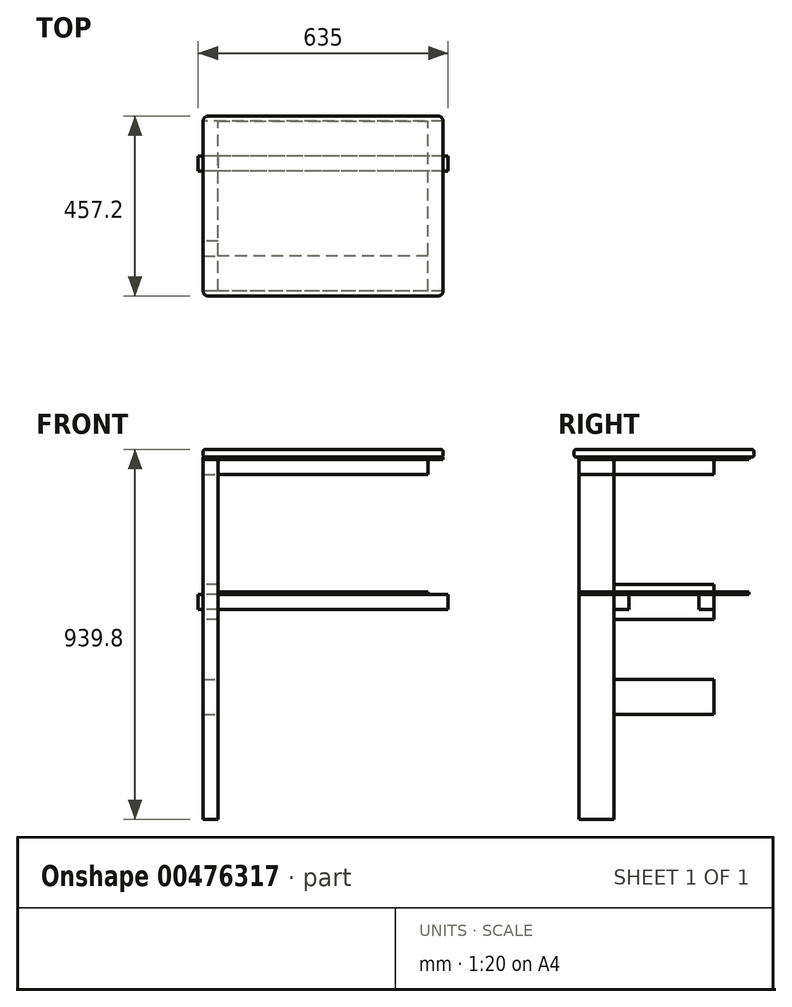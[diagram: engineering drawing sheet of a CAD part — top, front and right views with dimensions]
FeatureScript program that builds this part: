
annotation { "Feature Type Name" : "Feature", "Feature Type Description" : "" }
export const myFeature = defineFeature(function(context is Context, id is Id, definition is map)
    precondition{}
    {
        {
            var Q0;
            Q0=qCreatedBy(makeId("Top.planeOp"),FACE);
            var sketch = newSketch(context, id + "F0", { "sketchPlane" : qUnion([Q0])});
            skLineSegment(sketch, "E0.bottom", {"start": v(304.8, -215.9) * mm, "end": v(-304.8, -215.9) * mm});
            skLineSegment(sketch, "E0.top", {"start": v(304.8, 215.9) * mm, "end": v(-304.8, 215.9) * mm});
            skLineSegment(sketch, "E0.left", {"start": v(304.8, -215.9) * mm, "end": v(304.8, 215.9) * mm});
            skLineSegment(sketch, "E0.right", {"start": v(-304.8, -215.9) * mm, "end": v(-304.8, 215.9) * mm});
            skPoint(sketch, "E0.middle", {"position": v(0, 0) * mm});
            skSolve(sketch);
        }
        {
            var Q0;
            Q0 = qSketchRegion(id + "F0", true);
            extrude(context, id + "F1", {"entities" : qUnion([Q0]), "oppositeDirection" : true, "depth" : 6.35 * mm, "offsetDistance" : 25.4 * mm});
        }
        {
            var Q0;
            Q0=makeQuery(id+"F1.opExtrude","CAP_FACE",FACE,{"disambiguationData":[OSD([sQuery(id+"F0.wireOp",EDGE,"E0.bottom"),sQuery(id+"F0.wireOp",EDGE,"E0.top"),sQuery(id+"F0.wireOp",EDGE,"E0.left"),sQuery(id+"F0.wireOp",EDGE,"E0.right")])],"isStart":false});
            var sketch = newSketch(context, id + "F2", { "sketchPlane" : qUnion([Q0])});
            skLineSegment(sketch, "E1.bottom", {"start": v(-304.8, 215.9) * mm, "end": v(-266.7, 215.9) * mm});
            skLineSegment(sketch, "E1.top", {"start": v(-304.8, 127) * mm, "end": v(-266.7, 127) * mm});
            skLineSegment(sketch, "E1.left", {"start": v(-304.8, 215.9) * mm, "end": v(-304.8, 127) * mm});
            skLineSegment(sketch, "E1.right", {"start": v(-266.7, 215.9) * mm, "end": v(-266.7, 127) * mm});
            skSolve(sketch);
        }
        {
            var Q0;
            Q0 = qSketchRegion(id + "F2", true);
            extrude(context, id + "F3", {"entities" : qUnion([Q0]), "depth" : 914.4 * mm, "offsetDistance" : 25.4 * mm});
        }
        {
            var Q0;
            Q0=makeQuery(id+"F3.opExtrude","SWEPT_FACE",FACE,{"disambiguationData":[OSD([sQuery(id+"F2.wireOp",EDGE,"E1.right")])]});
            var sketch = newSketch(context, id + "F4", { "sketchPlane" : qUnion([Q0])});
            skLineSegment(sketch, "E2.bottom", {"start": v(-215.9, -6.35) * mm, "end": v(-127, -6.35) * mm});
            skLineSegment(sketch, "E2.top", {"start": v(-215.9, -44.45) * mm, "end": v(-127, -44.45) * mm});
            skLineSegment(sketch, "E2.left", {"start": v(-215.9, -6.35) * mm, "end": v(-215.9, -44.45) * mm});
            skLineSegment(sketch, "E2.right", {"start": v(-127, -6.35) * mm, "end": v(-127, -44.45) * mm});
            skSolve(sketch);
        }
        {
            var Q0;
            Q0 = qSketchRegion(id + "F4", true);
            extrude(context, id + "F5", {"entities" : qUnion([Q0]), "depth" : 533.4 * mm, "offsetDistance" : 25.4 * mm});
        }
        {
            var Q0;
            Q0=makeQuery(id+"F3.opExtrude","SWEPT_FACE",FACE,{"disambiguationData":[OSD([sQuery(id+"F2.wireOp",EDGE,"E1.top")])]});
            var sketch = newSketch(context, id + "F6", { "sketchPlane" : qUnion([Q0])});
            skLineSegment(sketch, "E3.bottom", {"start": v(304.8, -6.35) * mm, "end": v(266.7, -6.35) * mm});
            skLineSegment(sketch, "E3.top", {"start": v(304.8, -44.45) * mm, "end": v(266.7, -44.45) * mm});
            skLineSegment(sketch, "E3.left", {"start": v(304.8, -6.35) * mm, "end": v(304.8, -44.45) * mm});
            skLineSegment(sketch, "E3.right", {"start": v(266.7, -6.35) * mm, "end": v(266.7, -44.45) * mm});
            skSolve(sketch);
        }
        {
            var Q0;
            Q0 = qSketchRegion(id + "F6", true);
            extrude(context, id + "F7", {"entities" : qUnion([Q0]), "depth" : 254 * mm, "offsetDistance" : 25.4 * mm});
        }
        {
            var Q0;
            Q0=makeQuery(id+"F3.opExtrude","SWEPT_FACE",FACE,{"disambiguationData":[OSD([sQuery(id+"F2.wireOp",EDGE,"E1.top")])]});
            var sketch = newSketch(context, id + "F8", { "sketchPlane" : qUnion([Q0])});
            skLineSegment(sketch, "E4.bottom", {"start": v(304.8, -565.15) * mm, "end": v(266.7, -565.15) * mm});
            skLineSegment(sketch, "E4.top", {"start": v(304.8, -654.05) * mm, "end": v(266.7, -654.05) * mm});
            skLineSegment(sketch, "E4.left", {"start": v(304.8, -565.15) * mm, "end": v(304.8, -654.05) * mm});
            skLineSegment(sketch, "E4.right", {"start": v(266.7, -565.15) * mm, "end": v(266.7, -654.05) * mm});
            skSolve(sketch);
        }
        {
            var Q0;
            Q0 = qSketchRegion(id + "F8", true);
            extrude(context, id + "F9", {"entities" : qUnion([Q0]), "depth" : 254 * mm, "offsetDistance" : 25.4 * mm});
        }
        {
            var Q0;
            Q0=makeQuery(id+"F3.opExtrude","SWEPT_FACE",FACE,{"disambiguationData":[OSD([sQuery(id+"F2.wireOp",EDGE,"E1.left")])]});
            var sketch = newSketch(context, id + "F10", { "sketchPlane" : qUnion([Q0])});
            skLineSegment(sketch, "E5.bottom", {"start": v(127, -323.85) * mm, "end": v(-127, -323.85) * mm});
            skLineSegment(sketch, "E5.top", {"start": v(127, -412.75) * mm, "end": v(-127, -412.75) * mm});
            skLineSegment(sketch, "E5.left", {"start": v(127, -323.85) * mm, "end": v(127, -349.25) * mm});
            skLineSegment(sketch, "E5.right", {"start": v(-127, -323.85) * mm, "end": v(-127, -349.25) * mm});
            skLineSegment(sketch, "E6.bottom", {"start": v(-127, -349.25) * mm, "end": v(-88.9, -349.25) * mm});
            skLineSegment(sketch, "E6.top", {"start": v(-127, -387.35) * mm, "end": v(-88.9, -387.35) * mm});
            skLineSegment(sketch, "E6.right", {"start": v(-88.9, -349.25) * mm, "end": v(-88.9, -387.35) * mm});
            skLineSegment(sketch, "E7.bottom", {"start": v(127, -349.25) * mm, "end": v(88.9, -349.25) * mm});
            skLineSegment(sketch, "E7.top", {"start": v(127, -387.35) * mm, "end": v(88.9, -387.35) * mm});
            skLineSegment(sketch, "E7.right", {"start": v(88.9, -349.25) * mm, "end": v(88.9, -387.35) * mm});
            skLineSegment(sketch, "E8.trimOffspring", {"start": v(-127, -387.35) * mm, "end": v(-127, -412.75) * mm});
            skLineSegment(sketch, "E9.trimOffspring", {"start": v(127, -387.35) * mm, "end": v(127, -412.75) * mm});
            skSolve(sketch);
        }
        {
            var Q0;
            Q0 = qSketchRegion(id + "F10", true);
            extrude(context, id + "F11", {"entities" : qUnion([Q0]), "oppositeDirection" : true, "depth" : 38.1 * mm, "offsetDistance" : 25.4 * mm});
        }
        {
            var Q0;
            Q0=makeQuery(id+"F11.opExtrude","CAP_FACE",FACE,{"disambiguationData":[OSD([sQuery(id+"F10.wireOp",EDGE,"E5.bottom"),sQuery(id+"F10.wireOp",EDGE,"E5.top"),sQuery(id+"F10.wireOp",EDGE,"E5.left"),sQuery(id+"F10.wireOp",EDGE,"E5.right"),sQuery(id+"F10.wireOp",EDGE,"E6.bottom"),sQuery(id+"F10.wireOp",EDGE,"E6.top"),sQuery(id+"F10.wireOp",EDGE,"E6.right"),sQuery(id+"F10.wireOp",EDGE,"E7.bottom"),sQuery(id+"F10.wireOp",EDGE,"E7.top"),sQuery(id+"F10.wireOp",EDGE,"E7.right"),sQuery(id+"F10.wireOp",EDGE,"E8.trimOffspring"),sQuery(id+"F10.wireOp",EDGE,"E9.trimOffspring")])],"isStart":true});
            var sketch = newSketch(context, id + "F12", { "sketchPlane" : qUnion([Q0])});
            skLineSegment(sketch, "E10.bottom", {"start": v(-127, -349.25) * mm, "end": v(-88.9, -349.25) * mm});
            skLineSegment(sketch, "E10.top", {"start": v(-127, -387.35) * mm, "end": v(-88.9, -387.35) * mm});
            skLineSegment(sketch, "E10.left", {"start": v(-127, -349.25) * mm, "end": v(-127, -387.35) * mm});
            skLineSegment(sketch, "E10.right", {"start": v(-88.9, -349.25) * mm, "end": v(-88.9, -387.35) * mm});
            skSolve(sketch);
        }
        {
            var Q0;
            Q0 = qSketchRegion(id + "F12", true);
            extrude(context, id + "F13", {"entities" : qUnion([Q0]), "oppositeDirection" : true, "depth" : 622.3 * mm, "offsetDistance" : 25.4 * mm, "hasSecondDirection" : true, "secondDirectionOppositeDirection" : false, "secondDirectionDepth" : 12.7 * mm});
        }
        {
            var Q0;
            Q0=makeQuery(id+"F13.opExtrude","SWEPT_FACE",FACE,{"disambiguationData":[OSD([sQuery(id+"F12.wireOp",EDGE,"E10.bottom")])]});
            var sketch = newSketch(context, id + "F14", { "sketchPlane" : qUnion([Q0])});
            skLineSegment(sketch, "E11.bottom", {"start": v(-266.7, -215.9) * mm, "end": v(266.7, -215.9) * mm});
            skLineSegment(sketch, "E11.top", {"start": v(-266.7, 215.9) * mm, "end": v(266.7, 215.9) * mm});
            skLineSegment(sketch, "E11.left", {"start": v(-266.7, -215.9) * mm, "end": v(-266.7, 215.9) * mm});
            skLineSegment(sketch, "E11.right", {"start": v(266.7, -215.9) * mm, "end": v(266.7, 215.9) * mm});
            skSolve(sketch);
        }
        {
            var Q0;
            Q0 = qSketchRegion(id + "F14", true);
            extrude(context, id + "F15", {"entities" : qUnion([Q0]), "depth" : 6.35 * mm, "offsetDistance" : 25.4 * mm});
        }
        {
            var Q0;
            Q0=makeQuery(id+"F1.opExtrude","CAP_FACE",FACE,{"disambiguationData":[OSD([sQuery(id+"F0.wireOp",EDGE,"E0.bottom"),sQuery(id+"F0.wireOp",EDGE,"E0.top"),sQuery(id+"F0.wireOp",EDGE,"E0.left"),sQuery(id+"F0.wireOp",EDGE,"E0.right")])],"isStart":true});
            var sketch = newSketch(context, id + "F16", { "sketchPlane" : qUnion([Q0])});
            skLineSegment(sketch, "E12.bottom", {"start": v(304.8, -228.6) * mm, "end": v(-304.8, -228.6) * mm});
            skLineSegment(sketch, "E12.top", {"start": v(304.8, 228.6) * mm, "end": v(-304.8, 228.6) * mm});
            skLineSegment(sketch, "E12.left", {"start": v(304.8, -228.6) * mm, "end": v(304.8, 228.6) * mm});
            skLineSegment(sketch, "E12.right", {"start": v(-304.8, -228.6) * mm, "end": v(-304.8, 228.6) * mm});
            skPoint(sketch, "E12.middle", {"position": v(0, 0) * mm});
            skSolve(sketch);
        }
        {
            var Q0;
            Q0 = qSketchRegion(id + "F16", true);
            extrude(context, id + "F17", {"entities" : qUnion([Q0]), "depth" : 19.05 * mm, "offsetDistance" : 25.4 * mm});
        }
        {
            var Q0;
            Q0=makeQuery(id+"F17.opExtrude","SWEPT_EDGE",EDGE,{"disambiguationData":[OSD([sQuery(id+"F16.wireOp",EDGE,"E12.bottom"),sQuery(id+"F16.wireOp",EDGE,"E12.left")])]});
            var Q1;
            Q1=makeQuery(id+"F17.opExtrude","SWEPT_EDGE",EDGE,{"disambiguationData":[OSD([sQuery(id+"F16.wireOp",EDGE,"E12.bottom"),sQuery(id+"F16.wireOp",EDGE,"E12.right")])]});
            var Q2;
            Q2=makeQuery(id+"F17.opExtrude","SWEPT_EDGE",EDGE,{"disambiguationData":[OSD([sQuery(id+"F16.wireOp",EDGE,"E12.top"),sQuery(id+"F16.wireOp",EDGE,"E12.right")])]});
            var Q3;
            Q3=makeQuery(id+"F17.opExtrude","SWEPT_EDGE",EDGE,{"disambiguationData":[OSD([sQuery(id+"F16.wireOp",EDGE,"E12.top"),sQuery(id+"F16.wireOp",EDGE,"E12.left")])]});
            fillet(context, id + "F18", {"entities" : qUnion([Q0, Q1, Q2, Q3]), "radius" : 12.7 * mm, "tangentPropagation" : true, "allowEdgeOverflow" : false});
        }
        {
            var Q0;
            Q0=makeQuery(id+"F17.opExtrude","CAP_FACE",FACE,{"disambiguationData":[OSD([sQuery(id+"F16.wireOp",EDGE,"E12.bottom"),sQuery(id+"F16.wireOp",EDGE,"E12.top"),sQuery(id+"F16.wireOp",EDGE,"E12.left"),sQuery(id+"F16.wireOp",EDGE,"E12.right")])],"isStart":true});
            var Q1;
            Q1=makeQuery(id+"F17.opExtrude","CAP_FACE",FACE,{"disambiguationData":[OSD([sQuery(id+"F16.wireOp",EDGE,"E12.bottom"),sQuery(id+"F16.wireOp",EDGE,"E12.top"),sQuery(id+"F16.wireOp",EDGE,"E12.left"),sQuery(id+"F16.wireOp",EDGE,"E12.right")])],"isStart":false});
            fillet(context, id + "F19", {"entities" : qUnion([Q0, Q1]), "radius" : 5.08 * mm, "tangentPropagation" : true, "allowEdgeOverflow" : false});
        }
    });
